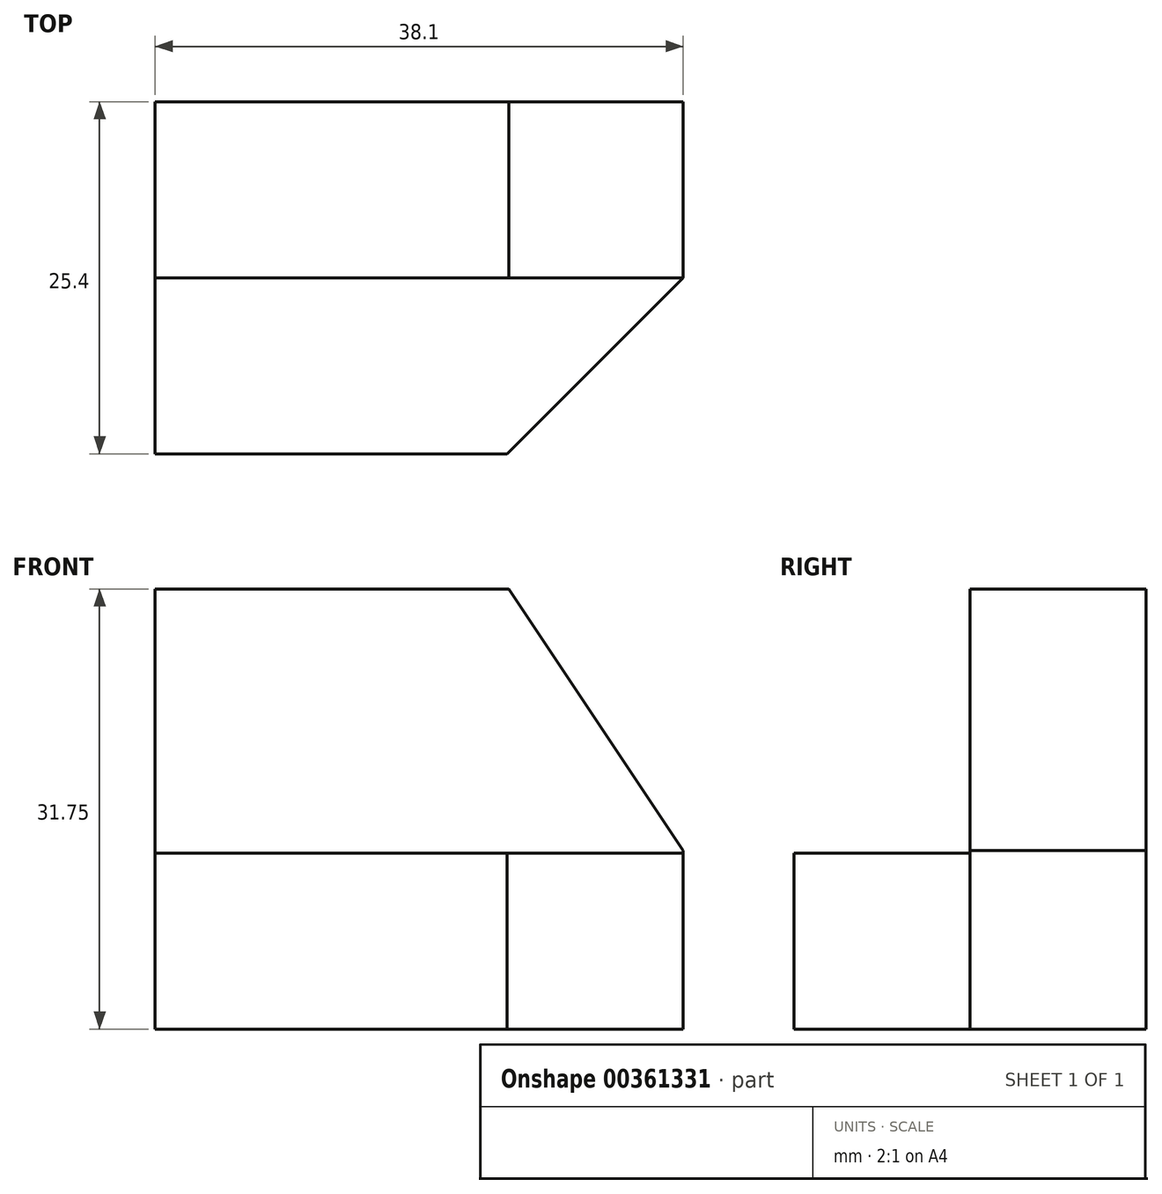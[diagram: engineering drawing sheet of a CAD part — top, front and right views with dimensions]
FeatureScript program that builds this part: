
annotation { "Feature Type Name" : "Feature", "Feature Type Description" : "" }
export const myFeature = defineFeature(function(context is Context, id is Id, definition is map)
    precondition{}
    {
        {
            var Q0;
            Q0=qCreatedBy(makeId("Right.planeOp"),FACE);
            var sketch = newSketch(context, id + "F0", { "sketchPlane" : qUnion([Q0])});
            skLineSegment(sketch, "E0", {"start": v(0, 12.7) * mm, "end": v(12.7, 12.7) * mm});
            skLineSegment(sketch, "E1", {"start": v(12.7, 12.7) * mm, "end": v(12.7, 31.75) * mm});
            skLineSegment(sketch, "E2", {"start": v(12.7, 31.75) * mm, "end": v(25.4, 31.75) * mm});
            skLineSegment(sketch, "E3", {"start": v(25.4, 31.75) * mm, "end": v(25.4, 0) * mm});
            skLineSegment(sketch, "E4", {"start": v(25.4, 0) * mm, "end": v(0, 0) * mm});
            skLineSegment(sketch, "E5", {"start": v(0, 0) * mm, "end": v(0, 12.7) * mm});
            skSolve(sketch);
        }
        {
            var Q0;
            Q0 = qSketchRegion(id + "F0", true);
            extrude(context, id + "F1", {"entities" : qUnion([Q0]), "oppositeDirection" : true, "depth" : 38.1 * mm});
        }
        {
            var Q0;
            Q0=makeQuery(id+"F1.opExtrude","SWEPT_FACE",FACE,{"disambiguationData":[OSD([sQuery(id+"F0.wireOp",EDGE,"E0")])]});
            var sketch = newSketch(context, id + "F2", { "sketchPlane" : qUnion([Q0])});
            skLineSegment(sketch, "E6", {"start": v(0, 12.7) * mm, "end": v(-12.7, 0) * mm});
            skLineSegment(sketch, "E7", {"start": v(-12.7, 0) * mm, "end": v(0, 0) * mm});
            skLineSegment(sketch, "E8", {"start": v(0, 0) * mm, "end": v(0, 12.7) * mm});
            skSolve(sketch);
        }
        {
            var Q0;
            Q0=makeQuery(id+"F2.imprint","IMPRINT",FACE,{"disambiguationData":[TD([[makeQuery(id+"F2.imprint","IMPRINT",EDGE,{"derivedFrom":sQuery(id+"F2.wireOp",EDGE,"E6")}),1.0]])]});
            extrude(context, id + "F3", {"entities" : qUnion([Q0]), "operationType" : NewBodyOperationType.REMOVE, "oppositeDirection" : true, "depth" : 12.7 * mm});
        }
        {
            var Q0;
            Q0=qCreatedBy(makeId("Front.planeOp"),FACE);
            var sketch = newSketch(context, id + "F4", { "sketchPlane" : qUnion([Q0])});
            skLineSegment(sketch, "E9", {"start": v(0, 12.88) * mm, "end": v(-12.7, 31.93) * mm});
            skLineSegment(sketch, "E10", {"start": v(-12.7, 31.93) * mm, "end": v(0, 31.93) * mm});
            skLineSegment(sketch, "E11", {"start": v(0, 31.93) * mm, "end": v(0, 12.88) * mm});
            skSolve(sketch);
        }
        {
            var Q0;
            Q0 = qSketchRegion(id + "F4", true);
            extrude(context, id + "F5", {"entities" : qUnion([Q0]), "operationType" : NewBodyOperationType.REMOVE, "oppositeDirection" : true, "depth" : 25.4 * mm});
        }
    });
